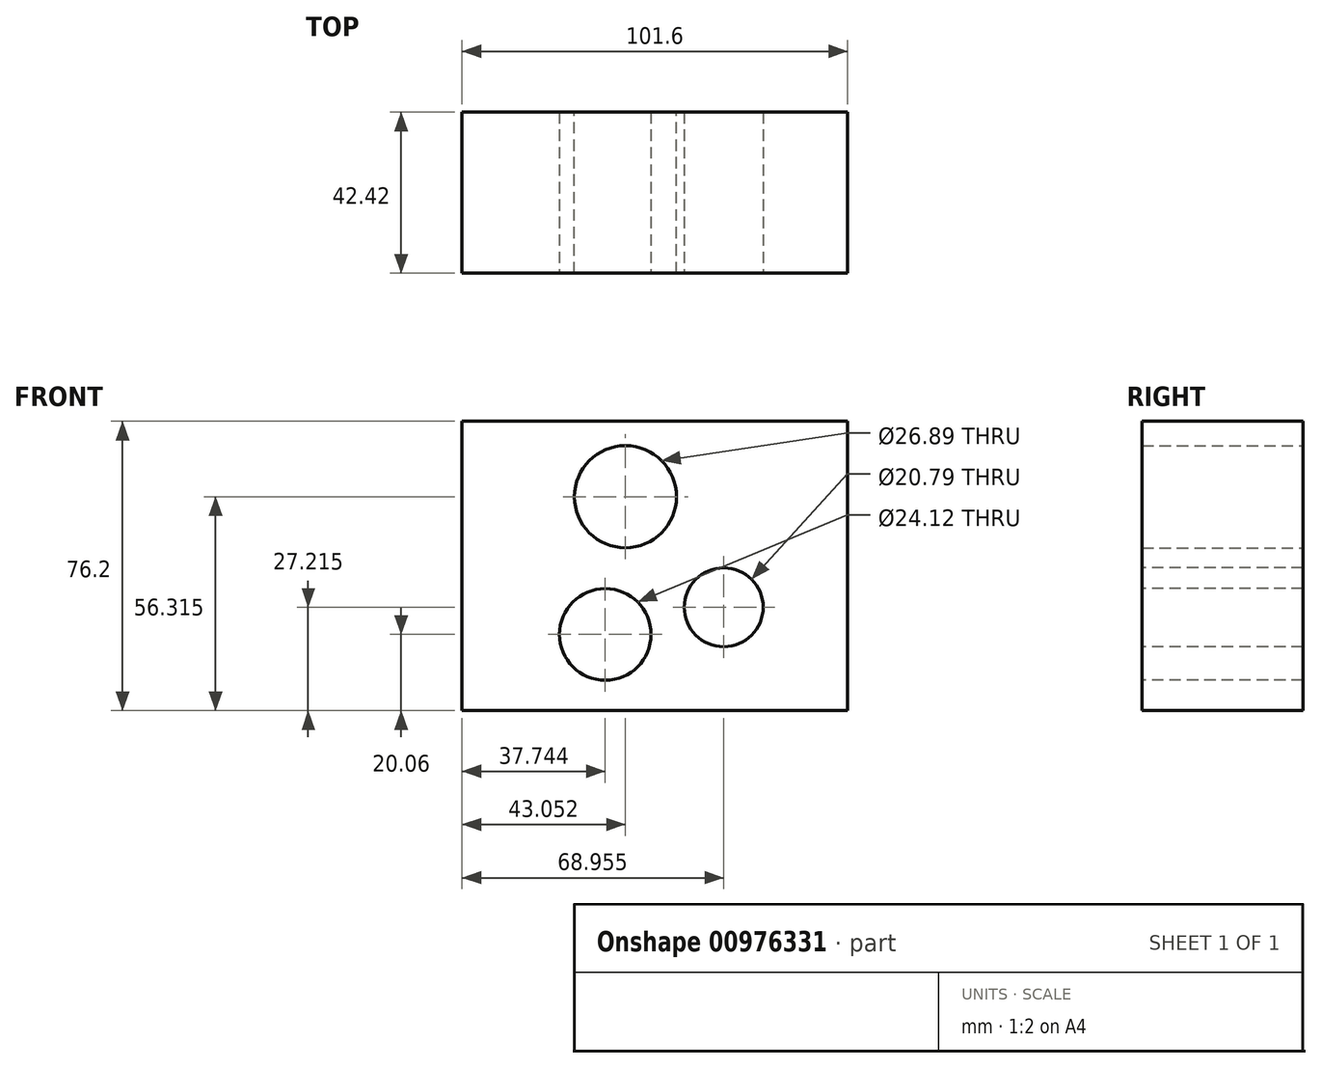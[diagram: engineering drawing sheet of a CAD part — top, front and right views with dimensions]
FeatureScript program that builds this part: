
annotation { "Feature Type Name" : "Feature", "Feature Type Description" : "" }
export const myFeature = defineFeature(function(context is Context, id is Id, definition is map)
    precondition{}
    {
        {
            var Q0;
            Q0=qCreatedBy(makeId("Front.planeOp"),FACE);
            var sketch = newSketch(context, id + "F0", { "sketchPlane" : qUnion([Q0])});
            skLineSegment(sketch, "E0.bottom", {"start": v(-24.04, 73.71) * mm, "end": v(77.56, 73.71) * mm});
            skLineSegment(sketch, "E0.top", {"start": v(-24.04, -2.49) * mm, "end": v(77.56, -2.49) * mm});
            skLineSegment(sketch, "E0.left", {"start": v(-24.04, 73.71) * mm, "end": v(-24.04, -2.49) * mm});
            skLineSegment(sketch, "E0.right", {"start": v(77.56, 73.71) * mm, "end": v(77.56, -2.49) * mm});
            skSolve(sketch);
        }
        {
            var Q0;
            Q0 = qSketchRegion(id + "F0", true);
            extrude(context, id + "F1", {"entities" : qUnion([Q0]), "depth" : 42.42 * mm, "offsetDistance" : 25.4 * mm});
        }
        {
            var Q0;
            Q0=qCreatedBy(makeId("Front.planeOp"),FACE);
            var sketch = newSketch(context, id + "F2", { "sketchPlane" : qUnion([Q0])});
            skCircle(sketch, "E1", {"center": v(19.01, 53.83) * mm, "radius": 13.44 * mm});
            skSolve(sketch);
        }
        {
            var Q0;
            Q0 = qSketchRegion(id + "F2", true);
            extrude(context, id + "F3", {"entities" : qUnion([Q0]), "operationType" : NewBodyOperationType.REMOVE, "depth" : 67.56 * mm, "offsetDistance" : 25.4 * mm});
        }
        {
            var Q0;
            Q0=makeQuery(id+"F1.opExtrude","CAP_FACE",FACE,{"disambiguationData":[OSD([sQuery(id+"F0.wireOp",EDGE,"E0.bottom"),sQuery(id+"F0.wireOp",EDGE,"E0.top"),sQuery(id+"F0.wireOp",EDGE,"E0.left"),sQuery(id+"F0.wireOp",EDGE,"E0.right")])],"isStart":false});
            var sketch = newSketch(context, id + "F4", { "sketchPlane" : qUnion([Q0])});
            skCircle(sketch, "E2", {"center": v(44.92, 24.72) * mm, "radius": 10.4 * mm});
            skPoint(sketch, "E2.first.point", {"position": v(34.99, 27.8) * mm});
            skPoint(sketch, "E2.second.point", {"position": v(49.64, 15.47) * mm});
            skPoint(sketch, "E2.third.point", {"position": v(48.94, 34.3) * mm});
            skSolve(sketch);
        }
        {
            var Q0;
            Q0 = qSketchRegion(id + "F4", true);
            extrude(context, id + "F5", {"entities" : qUnion([Q0]), "operationType" : NewBodyOperationType.REMOVE, "oppositeDirection" : true, "depth" : 93.22 * mm, "offsetDistance" : 25.4 * mm});
        }
        {
            var Q0;
            Q0=makeQuery(id+"F1.opExtrude","CAP_FACE",FACE,{"disambiguationData":[OSD([sQuery(id+"F0.wireOp",EDGE,"E0.bottom"),sQuery(id+"F0.wireOp",EDGE,"E0.top"),sQuery(id+"F0.wireOp",EDGE,"E0.left"),sQuery(id+"F0.wireOp",EDGE,"E0.right")])],"isStart":false});
            var sketch = newSketch(context, id + "F6", { "sketchPlane" : qUnion([Q0])});
            skCircle(sketch, "E3", {"center": v(13.7, 17.57) * mm, "radius": 12.06 * mm});
            skPoint(sketch, "E3.first.point", {"position": v(7.3, 27.8) * mm});
            skPoint(sketch, "E3.second.point", {"position": v(25.68, 16.16) * mm});
            skPoint(sketch, "E3.third.point", {"position": v(20.1, 27.8) * mm});
            skSolve(sketch);
        }
        {
            var Q0;
            Q0 = qSketchRegion(id + "F6", true);
            extrude(context, id + "F7", {"entities" : qUnion([Q0]), "operationType" : NewBodyOperationType.REMOVE, "oppositeDirection" : true, "depth" : 66.55 * mm, "offsetDistance" : 25.4 * mm});
        }
    });
